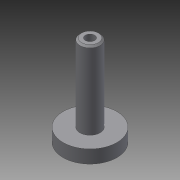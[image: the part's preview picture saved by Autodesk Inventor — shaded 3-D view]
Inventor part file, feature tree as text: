
AUTODESK INVENTOR PART (.ipt)
format: ipt  version: 2014 (Build 180170000, 170)  size: 102,912 bytes
history: native  units: mm
features: extrude x3, sketch x3, chamfer x1
ambient origin geometry x8: Origin, YZ Plane, XZ Plane, XY Plane, X Axis, Y Axis, Z Axis, Center Point
bodies: Solid1 (feature_tree)
feature tree (7):
  extrude  "Extrusion1"  Depth=7.8mm TaperAngle=0.0deg
  extrude  "Extrusion2"  Depth=46.0mm TaperAngle=0.0deg
  extrude  "Extrusion3"  Depth=15.0mm TaperAngle=0.0deg
  chamfer  "Chamfer1"  Distance=1.0mm Angle=45.0deg
  sketch  "Sketch1"  dims[d0=32.0mm d1=7.8mm d2=0.0mm]
  sketch  "Sketch2"  dims[d3=12.0mm d4=46.0mm d5=0.0mm]
  sketch  "Sketch3"  dims[d6=5.5mm d7=15.0mm d8=0.0mm d9=1.0mm d10=2.0mm d11=45.0deg]
